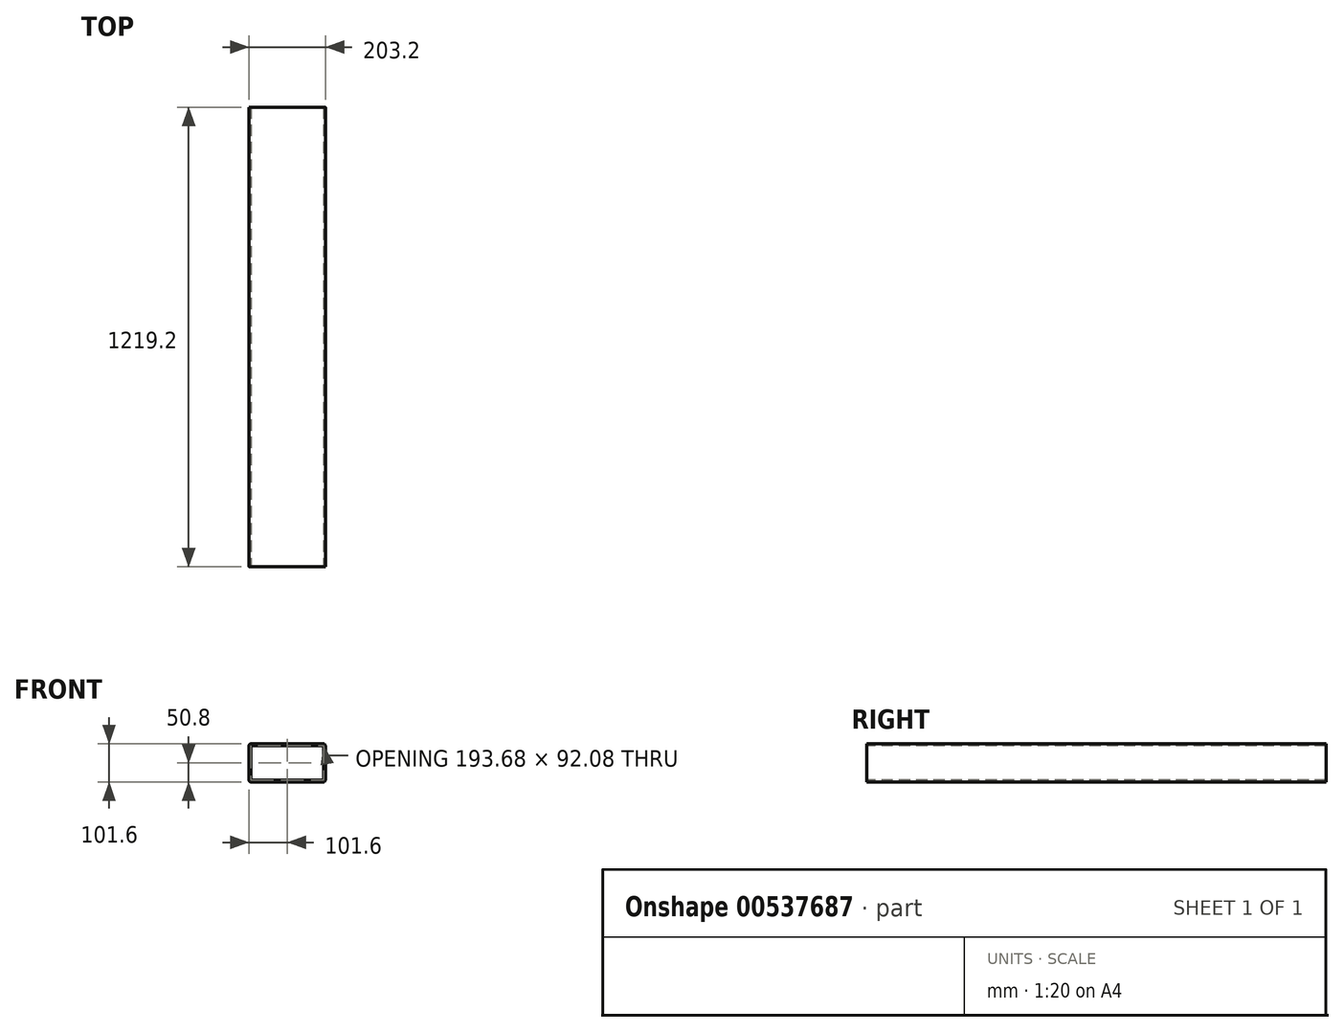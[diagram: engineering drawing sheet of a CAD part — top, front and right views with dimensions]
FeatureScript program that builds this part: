
annotation { "Feature Type Name" : "Feature", "Feature Type Description" : "" }
export const myFeature = defineFeature(function(context is Context, id is Id, definition is map)
    precondition{}
    {
        {
            var Q0;
            Q0=qCreatedBy(makeId("Front.planeOp"),FACE);
            var sketch = newSketch(context, id + "F0", { "sketchPlane" : qUnion([Q0])});
            skLineSegment(sketch, "E0.bottom", {"start": v(90.49, 46.04) * mm, "end": v(-90.49, 46.04) * mm});
            skLineSegment(sketch, "E0.top", {"start": v(90.49, -46.04) * mm, "end": v(-90.49, -46.04) * mm});
            skLineSegment(sketch, "E0.left", {"start": v(96.84, 39.69) * mm, "end": v(96.84, -39.69) * mm});
            skLineSegment(sketch, "E0.right", {"start": v(-96.84, 39.69) * mm, "end": v(-96.84, -39.69) * mm});
            skPoint(sketch, "E0.middle", {"position": v(0, 0) * mm});
            skLineSegment(sketch, "E1.bottom", {"start": v(95.25, 50.8) * mm, "end": v(-95.25, 50.8) * mm});
            skLineSegment(sketch, "E1.top", {"start": v(95.25, -50.8) * mm, "end": v(-95.25, -50.8) * mm});
            skLineSegment(sketch, "E1.left", {"start": v(101.6, 44.45) * mm, "end": v(101.6, -44.45) * mm});
            skLineSegment(sketch, "E1.right", {"start": v(-101.6, 44.45) * mm, "end": v(-101.6, -44.45) * mm});
            skPoint(sketch, "E2.visualSharp", {"position": v(-96.84, 46.04) * mm});
            skArc(sketch, "E2.filletArc", {"start": v(-90.49, 46.04) * mm, "mid": v(-94.98, 44.18) * mm, "end": v(-96.84, 39.69) * mm});
            skPoint(sketch, "E3.visualSharp", {"position": v(-101.6, 50.8) * mm});
            skArc(sketch, "E3.filletArc", {"start": v(-95.25, 50.8) * mm, "mid": v(-99.74, 48.94) * mm, "end": v(-101.6, 44.45) * mm});
            skPoint(sketch, "E4.visualSharp", {"position": v(96.84, 46.04) * mm});
            skArc(sketch, "E4.filletArc", {"start": v(96.84, 39.69) * mm, "mid": v(94.98, 44.18) * mm, "end": v(90.49, 46.04) * mm});
            skPoint(sketch, "E5.visualSharp", {"position": v(101.6, 50.8) * mm});
            skArc(sketch, "E5.filletArc", {"start": v(101.6, 44.45) * mm, "mid": v(99.74, 48.94) * mm, "end": v(95.25, 50.8) * mm});
            skPoint(sketch, "E6.visualSharp", {"position": v(96.84, -46.04) * mm});
            skArc(sketch, "E6.filletArc", {"start": v(90.49, -46.04) * mm, "mid": v(94.98, -44.18) * mm, "end": v(96.84, -39.69) * mm});
            skPoint(sketch, "E7.visualSharp", {"position": v(101.6, -50.8) * mm});
            skArc(sketch, "E7.filletArc", {"start": v(95.25, -50.8) * mm, "mid": v(99.74, -48.94) * mm, "end": v(101.6, -44.45) * mm});
            skPoint(sketch, "E8.visualSharp", {"position": v(-101.6, -50.8) * mm});
            skArc(sketch, "E8.filletArc", {"start": v(-101.6, -44.45) * mm, "mid": v(-99.74, -48.94) * mm, "end": v(-95.25, -50.8) * mm});
            skPoint(sketch, "E9.visualSharp", {"position": v(-96.84, -46.04) * mm});
            skArc(sketch, "E9.filletArc", {"start": v(-96.84, -39.69) * mm, "mid": v(-94.98, -44.18) * mm, "end": v(-90.49, -46.04) * mm});
            skSolve(sketch);
        }
        {
            var Q0;
            Q0 = qSketchRegion(id + "F0", true);
            extrude(context, id + "F1", {"entities" : qUnion([Q0]), "oppositeDirection" : true, "depth" : 1219.2 * mm, "offsetDistance" : 25.4 * mm});
        }
    });
